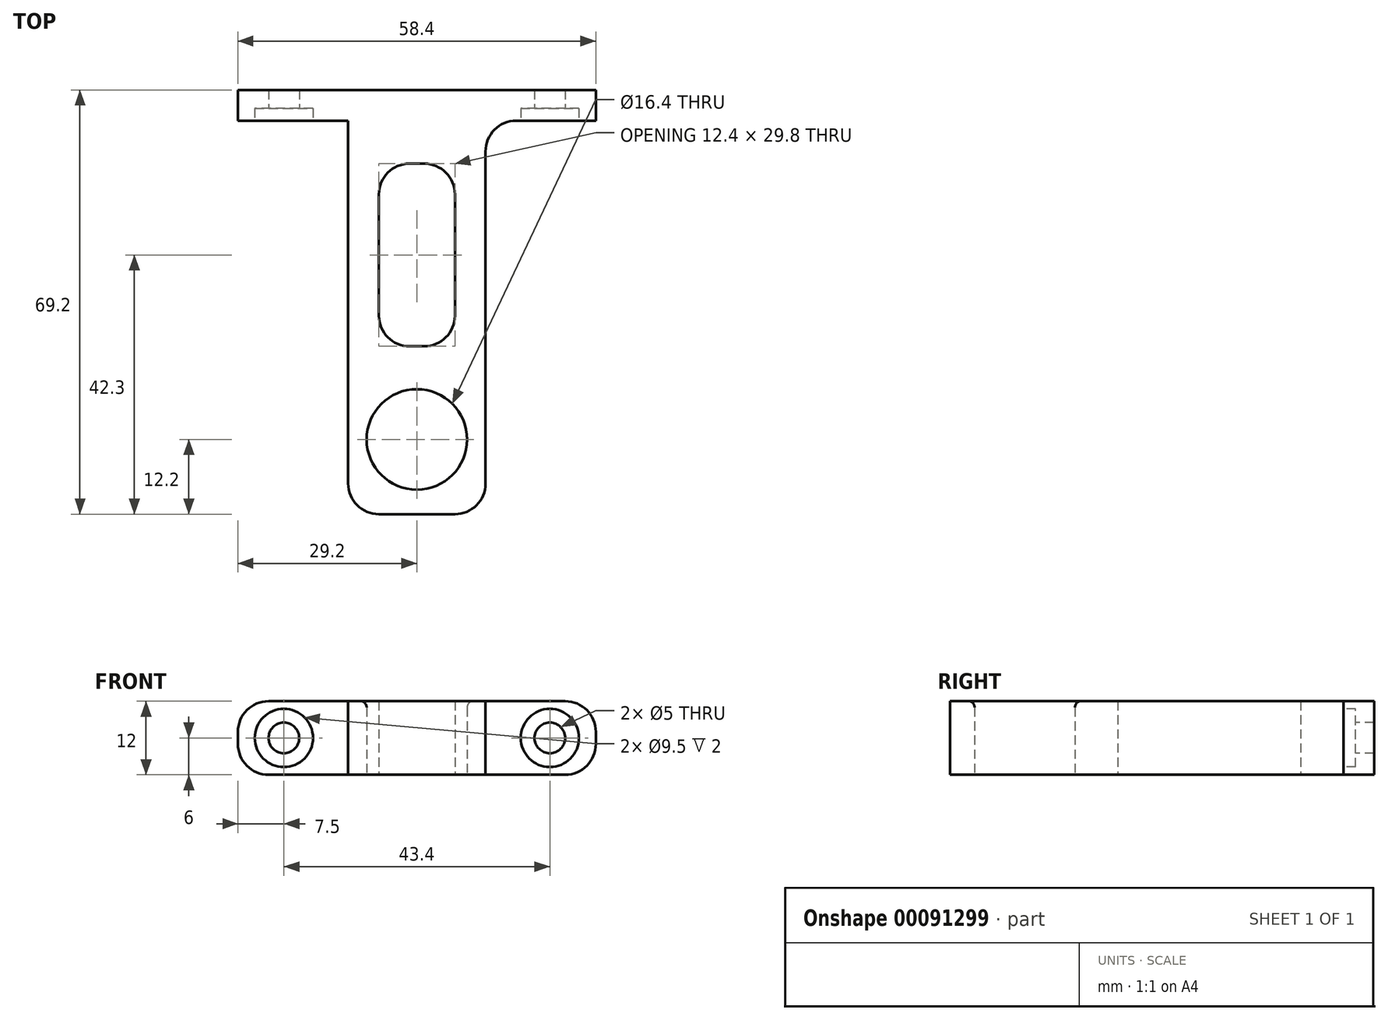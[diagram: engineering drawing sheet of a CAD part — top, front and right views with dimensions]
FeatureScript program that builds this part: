
annotation { "Feature Type Name" : "Feature", "Feature Type Description" : "" }
export const myFeature = defineFeature(function(context is Context, id is Id, definition is map)
    precondition{}
    {
        {
            var Q0;
            Q0=qCreatedBy(makeId("Top.planeOp"),FACE);
            var sketch = newSketch(context, id + "F0", { "sketchPlane" : qUnion([Q0])});
            skCircle(sketch, "E0", {"center": v(0, 0) * mm, "radius": 8.2 * mm});
            skLineSegment(sketch, "E1", {"start": v(-8.2, 52) * mm, "end": v(-8.2, 0) * mm, "construction": true});
            skLineSegment(sketch, "E2", {"start": v(-11.2, 52) * mm, "end": v(-11.2, 0) * mm});
            skLineSegment(sketch, "E3", {"start": v(-11.2, 0) * mm, "end": v(-8.2, 0) * mm});
            skLineSegment(sketch, "E4", {"start": v(-11.2, 0) * mm, "end": v(-11.2, -12.2) * mm});
            skLineSegment(sketch, "E5", {"start": v(-11.2, -12.2) * mm, "end": v(0, -12.2) * mm});
            skLineSegment(sketch, "E6", {"start": v(0, 42.96) * mm, "end": v(0, -49.62) * mm, "construction": true});
            skLineSegment(sketch, "E7", {"start": v(-11.2, 52) * mm, "end": v(0, 52) * mm});
            skLineSegment(sketch, "E8.MirrorCS", {"start": v(8.2, 52) * mm, "end": v(8.2, 0) * mm, "construction": true});
            skLineSegment(sketch, "E9.MirrorCS", {"start": v(11.2, 52) * mm, "end": v(0, 52) * mm});
            skLineSegment(sketch, "E10.MirrorCS", {"start": v(11.2, 52) * mm, "end": v(11.2, 0) * mm});
            skLineSegment(sketch, "E11.MirrorCS", {"start": v(11.2, -12.2) * mm, "end": v(0, -12.2) * mm});
            skLineSegment(sketch, "E12.MirrorCS", {"start": v(11.2, 0) * mm, "end": v(8.2, 0) * mm});
            skLineSegment(sketch, "E13.MirrorCS", {"start": v(11.2, 0) * mm, "end": v(11.2, -12.2) * mm});
            skLineSegment(sketch, "E14.bottom", {"start": v(-6.2, 45) * mm, "end": v(6.2, 45) * mm});
            skLineSegment(sketch, "E14.top", {"start": v(-6.2, 15.2) * mm, "end": v(6.2, 15.2) * mm});
            skLineSegment(sketch, "E14.left", {"start": v(-6.2, 45) * mm, "end": v(-6.2, 15.2) * mm});
            skLineSegment(sketch, "E14.right", {"start": v(6.2, 45) * mm, "end": v(6.2, 15.2) * mm});
            skPoint(sketch, "E15", {"position": v(0, 45) * mm});
            skSolve(sketch);
        }
        {
            var Q0;
            Q0=makeQuery(id+"F0.imprint","IMPRINT",FACE,{"disambiguationData":[TD([[makeQuery(id+"F0.imprint","IMPRINT",EDGE,{"derivedFrom":sQuery(id+"F0.wireOp",EDGE,"E2")}),1.0]])]});
            var Q1;
            {var subQ0=sQuery(id+"F0.wireOp",EDGE,"E11.MirrorCS");Q1=makeQuery(id+"F0.imprint","IMPRINT",FACE,{"disambiguationData":[TD([[makeQuery(id+"F0.imprint","IMPRINT",EDGE,{"derivedFrom":subQ0}),-1.0]])]});}
            var Q2;
            {var subQ0=sQuery(id+"F0.wireOp",EDGE,"E3");Q2=makeQuery(id+"F0.imprint","IMPRINT",FACE,{"disambiguationData":[TD([[makeQuery(id+"F0.imprint","IMPRINT",EDGE,{"derivedFrom":subQ0}),-1.0]])]});}
            extrude(context, id + "F1", {"entities" : qUnion([Q0, Q1, Q2]), "depth" : 12 * mm});
        }
        {
            var Q0;
            Q0=makeQuery(id+"F1.opExtrude","SWEPT_FACE",FACE,{"disambiguationData":[OSD([sQuery(id+"F0.wireOp",EDGE,"E7"),sQuery(id+"F0.wireOp",EDGE,"E9.MirrorCS")])]});
            var sketch = newSketch(context, id + "F2", { "sketchPlane" : qUnion([Q0])});
            skPoint(sketch, "E16.middle", {"position": v(0, 6) * mm});
            skPoint(sketch, "E16.middle.positionSnap0", {"position": v(0, 0) * mm});
            skPoint(sketch, "E16.middle.positionSnap1", {"position": v(-11.2, 6) * mm});
            skPoint(sketch, "E16.centerSnap0", {"position": v(0, 0) * mm});
            skPoint(sketch, "E16.centerSnap1", {"position": v(-11.2, 6) * mm});
            skLineSegment(sketch, "E17", {"start": v(-27.12, 6) * mm, "end": v(24.39, 6) * mm, "construction": true});
            skPoint(sketch, "E17.endSnap0", {"position": v(23, 6) * mm});
            skCircle(sketch, "E18", {"center": v(-21.7, 6) * mm, "radius": 2.5 * mm});
            skLineSegment(sketch, "E19", {"start": v(0, 20.6) * mm, "end": v(0, -8.6) * mm, "construction": true});
            skPoint(sketch, "E19.startSnap0", {"position": v(0, 16.77) * mm});
            skPoint(sketch, "E19.endSnap0", {"position": v(0, -7.21) * mm});
            skLineSegment(sketch, "E20.bottom", {"start": v(-29.2, 12) * mm, "end": v(29.2, 12) * mm});
            skLineSegment(sketch, "E20.top", {"start": v(-29.2, 0) * mm, "end": v(29.2, 0) * mm});
            skLineSegment(sketch, "E20.left", {"start": v(-29.2, 12) * mm, "end": v(-29.2, 0) * mm});
            skLineSegment(sketch, "E20.right", {"start": v(29.2, 12) * mm, "end": v(29.2, 0) * mm});
            skCircle(sketch, "E21.MirrorC", {"center": v(21.7, 6) * mm, "radius": 2.5 * mm});
            skSolve(sketch);
        }
        {
            var Q0;
            Q0 = qSketchRegion(id + "F2", true);
            extrude(context, id + "F3", {"entities" : qUnion([Q0]), "operationType" : NewBodyOperationType.ADD, "depth" : 5 * mm});
        }
        {
            var Q0;
            Q0=makeQuery(id+"F3.opExtrude","SWEPT_EDGE",EDGE,{"disambiguationData":[OSD([sQuery(id+"F2.wireOp",EDGE,"E16.bottom"),sQuery(id+"F2.wireOp",EDGE,"E16.right")])]});
            var Q1;
            Q1=makeQuery(id+"F3.opExtrude","SWEPT_EDGE",EDGE,{"disambiguationData":[OSD([sQuery(id+"F2.wireOp",EDGE,"E16.top"),sQuery(id+"F2.wireOp",EDGE,"E16.right")])]});
            var Q2;
            Q2=makeQuery(id+"F3.opExtrude","SWEPT_EDGE",EDGE,{"disambiguationData":[OSD([sQuery(id+"F2.wireOp",EDGE,"E16.bottom"),sQuery(id+"F2.wireOp",EDGE,"E16.left")])]});
            var Q3;
            Q3=makeQuery(id+"F3.opExtrude","SWEPT_EDGE",EDGE,{"disambiguationData":[OSD([sQuery(id+"F2.wireOp",EDGE,"E16.top"),sQuery(id+"F2.wireOp",EDGE,"E16.left")])]});
            var Q4;
            Q4=makeQuery(id+"F1.opExtrude","SWEPT_EDGE",EDGE,{"disambiguationData":[OSD([sQuery(id+"F0.wireOp",EDGE,"E4"),sQuery(id+"F0.wireOp",EDGE,"E5")])]});
            var Q5;
            Q5=makeQuery(id+"F1.opExtrude","SWEPT_EDGE",EDGE,{"disambiguationData":[OSD([sQuery(id+"F0.wireOp",EDGE,"E11.MirrorCS"),sQuery(id+"F0.wireOp",EDGE,"E13.MirrorCS")])]});
            fillet(context, id + "F4", {"entities" : qUnion([Q0, Q1, Q2, Q3, Q4, Q5]), "radius" : 5 * mm, "tangentPropagation" : true, "allowEdgeOverflow" : false});
        }
        {
            var Q0;
            Q0=makeQuery(id+"F1.opExtrude","SWEPT_EDGE",EDGE,{"disambiguationData":[OSD([sQuery(id+"F0.wireOp",EDGE,"E9.MirrorCS"),sQuery(id+"F0.wireOp",EDGE,"E10.MirrorCS")])]});
            var Q1;
            Q1=makeQuery(id+"F1.opExtrude","SWEPT_EDGE",EDGE,{"disambiguationData":[OSD([sQuery(id+"F0.wireOp",EDGE,"E2"),sQuery(id+"F0.wireOp",EDGE,"E7")])]});
            fillet(context, id + "F5", {"entities" : qUnion([Q0, Q1]), "radius" : 5 * mm, "tangentPropagation" : true, "allowEdgeOverflow" : false});
        }
        {
            var Q0;
            Q0=makeQuery(id+"F3.opExtrude","SWEPT_EDGE",EDGE,{"disambiguationData":[OSD([sQuery(id+"F2.wireOp",EDGE,"E20.bottom"),sQuery(id+"F2.wireOp",EDGE,"E20.right")])]});
            var Q1;
            Q1=makeQuery(id+"F3.opExtrude","SWEPT_EDGE",EDGE,{"disambiguationData":[OSD([sQuery(id+"F2.wireOp",EDGE,"E20.top"),sQuery(id+"F2.wireOp",EDGE,"E20.right")])]});
            var Q2;
            Q2=makeQuery(id+"F3.opExtrude","SWEPT_EDGE",EDGE,{"disambiguationData":[OSD([sQuery(id+"F2.wireOp",EDGE,"E20.top"),sQuery(id+"F2.wireOp",EDGE,"E20.left")])]});
            var Q3;
            Q3=makeQuery(id+"F3.opExtrude","SWEPT_EDGE",EDGE,{"disambiguationData":[OSD([sQuery(id+"F2.wireOp",EDGE,"E20.bottom"),sQuery(id+"F2.wireOp",EDGE,"E20.left")])]});
            fillet(context, id + "F6", {"entities" : qUnion([Q0, Q1, Q2, Q3]), "radius" : 5 * mm, "tangentPropagation" : true, "allowEdgeOverflow" : false});
        }
        {
            var Q0;
            {var subQ9=sQuery(id+"F2.wireOp",EDGE,"E18");var subQ10=sQuery(id+"F2.wireOp",EDGE,"E20.left");var subQ11=sQuery(id+"F2.wireOp",EDGE,"E20.bottom");var subQ12=sQuery(id+"F2.wireOp",EDGE,"E20.top");Q0=makeQuery(id+"F3.boolean.opBoolean","SPLIT",FACE,{"disambiguationData":[TD([makeQuery(id+"F3.opExtrude","SWEPT_FACE",FACE,{"disambiguationData":[OSD([subQ9])]})])],"derivedFrom":makeQuery(id+"F3.opExtrude","CAP_FACE",FACE,{"disambiguationData":[OSD([subQ9,subQ11,subQ12,subQ10,sQuery(id+"F2.wireOp",EDGE,"E20.right"),sQuery(id+"F2.wireOp",EDGE,"E21.MirrorC")])],"isStart":true})});}
            var sketch = newSketch(context, id + "F7", { "sketchPlane" : qUnion([Q0])});
            skCircle(sketch, "E22", {"center": v(21.7, 6) * mm, "radius": 4.75 * mm});
            skCircle(sketch, "E23.MirrorC", {"center": v(-21.7, 6) * mm, "radius": 4.75 * mm});
            skSolve(sketch);
        }
        {
            var Q0;
            Q0 = qSketchRegion(id + "F7", true);
            extrude(context, id + "F8", {"entities" : qUnion([Q0]), "operationType" : NewBodyOperationType.REMOVE, "oppositeDirection" : true, "depth" : 2 * mm});
        }
        {
            var Q0;
            Q0=makeQuery(id+"F1.opExtrude","CAP_EDGE",EDGE,{"disambiguationData":[OSD([sQuery(id+"F0.wireOp",EDGE,"E0")])],"isStart":false});
            fillet(context, id + "F9", {"entities" : qUnion([Q0]), "radius" : 1 * mm, "tangentPropagation" : true, "allowEdgeOverflow" : false});
        }
        {
            var Q0;
            Q0=makeQuery(id+"F1.opExtrude","SWEPT_EDGE",EDGE,{"disambiguationData":[OSD([sQuery(id+"F0.wireOp",EDGE,"E14.bottom"),sQuery(id+"F0.wireOp",EDGE,"E14.left")])]});
            var Q1;
            Q1=makeQuery(id+"F1.opExtrude","SWEPT_EDGE",EDGE,{"disambiguationData":[OSD([sQuery(id+"F0.wireOp",EDGE,"E14.bottom"),sQuery(id+"F0.wireOp",EDGE,"E14.right")])]});
            var Q2;
            Q2=makeQuery(id+"F1.opExtrude","SWEPT_EDGE",EDGE,{"disambiguationData":[OSD([sQuery(id+"F0.wireOp",EDGE,"E14.top"),sQuery(id+"F0.wireOp",EDGE,"E14.left")])]});
            var Q3;
            Q3=makeQuery(id+"F1.opExtrude","SWEPT_EDGE",EDGE,{"disambiguationData":[OSD([sQuery(id+"F0.wireOp",EDGE,"E14.top"),sQuery(id+"F0.wireOp",EDGE,"E14.right")])]});
            fillet(context, id + "F10", {"entities" : qUnion([Q0, Q1, Q2, Q3]), "radius" : 5 * mm, "tangentPropagation" : true, "allowEdgeOverflow" : false});
        }
        {
            var Q0;
            Q0=makeQuery(id+"F3.boolean.opBoolean","MERGE",FACE,{"derivedFrom":[makeQuery(id+"F1.opExtrude","CAP_FACE",FACE,{"disambiguationData":[OSD([sQuery(id+"F0.wireOp",EDGE,"E0"),sQuery(id+"F0.wireOp",EDGE,"E2"),sQuery(id+"F0.wireOp",EDGE,"E4"),sQuery(id+"F0.wireOp",EDGE,"E5"),sQuery(id+"F0.wireOp",EDGE,"E7"),sQuery(id+"F0.wireOp",EDGE,"E9.MirrorCS"),sQuery(id+"F0.wireOp",EDGE,"E10.MirrorCS"),sQuery(id+"F0.wireOp",EDGE,"E11.MirrorCS"),sQuery(id+"F0.wireOp",EDGE,"E13.MirrorCS"),sQuery(id+"F0.wireOp",EDGE,"E14.bottom"),sQuery(id+"F0.wireOp",EDGE,"E14.top"),sQuery(id+"F0.wireOp",EDGE,"E14.left"),sQuery(id+"F0.wireOp",EDGE,"E14.right")])],"isStart":false}),makeQuery(id+"F3.opExtrude","SWEPT_FACE",FACE,{"disambiguationData":[OSD([sQuery(id+"F2.wireOp",EDGE,"E20.bottom")])]})]});
            var sketch = newSketch(context, id + "F11", { "sketchPlane" : qUnion([Q0])});
            skLineSegment(sketch, "E24", {"start": v(-3.2, 11.51) * mm, "end": v(-11.2, 0) * mm, "construction": true});
            skPoint(sketch, "E25.0", {"position": v(-11.2, 0) * mm});
            skSolve(sketch);
        }
    });
